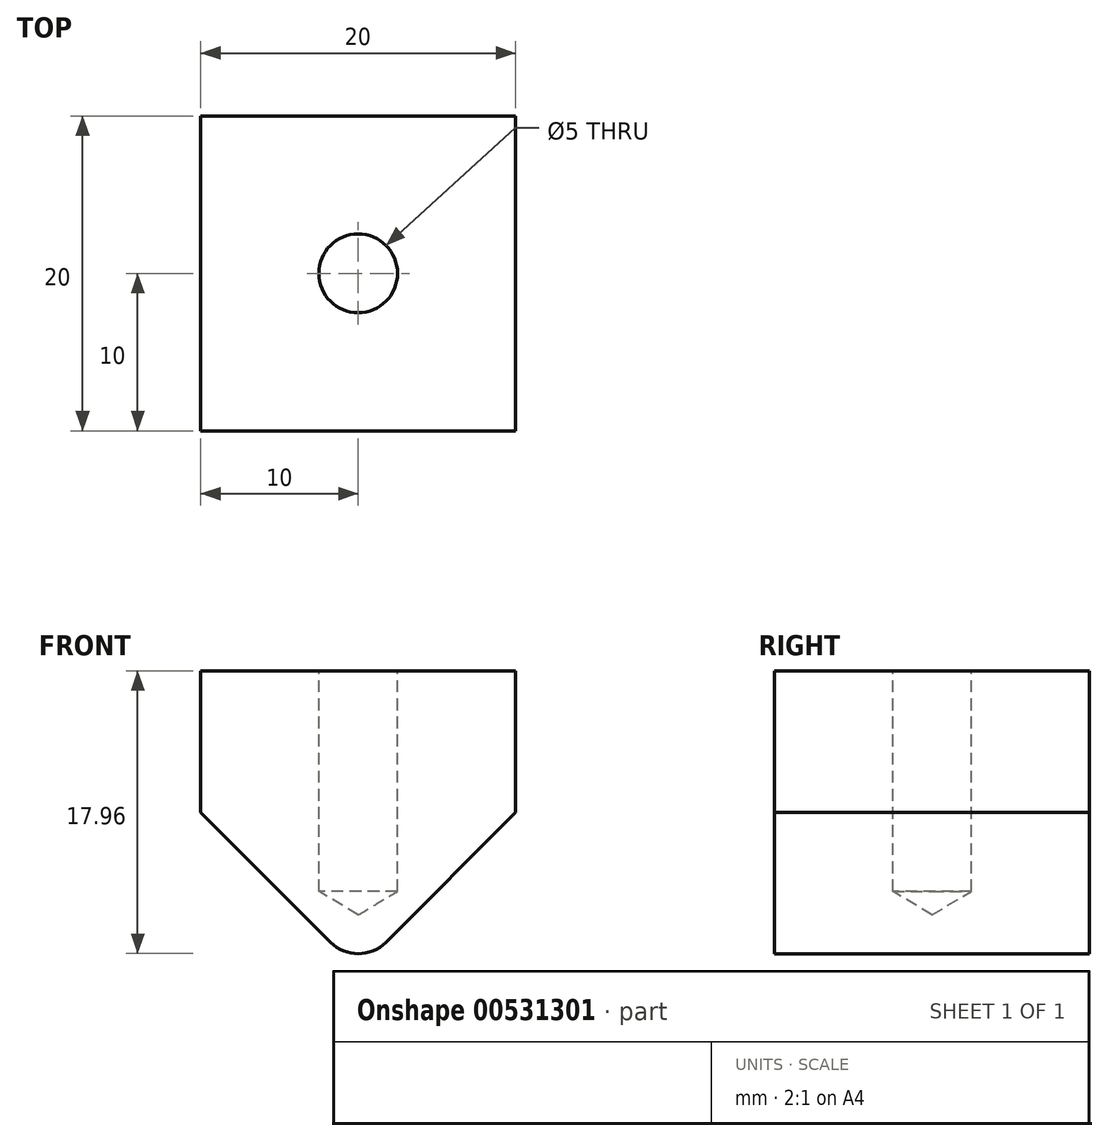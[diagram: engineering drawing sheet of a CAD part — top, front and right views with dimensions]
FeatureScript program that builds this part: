
annotation { "Feature Type Name" : "Feature", "Feature Type Description" : "" }
export const myFeature = defineFeature(function(context is Context, id is Id, definition is map)
    precondition{}
    {
        {
            var Q0;
            Q0=qCreatedBy(makeId("Front.planeOp"),FACE);
            var sketch = newSketch(context, id + "F0", { "sketchPlane" : qUnion([Q0])});
            skLineSegment(sketch, "E0", {"start": v(-14.02, 11.64) * mm, "end": v(5.98, 11.64) * mm});
            skLineSegment(sketch, "E1", {"start": v(5.98, 2.64) * mm, "end": v(5.98, 11.64) * mm});
            skLineSegment(sketch, "E2", {"start": v(5.98, 2.64) * mm, "end": v(-2.25, -5.6) * mm});
            skLineSegment(sketch, "E3", {"start": v(-5.79, -5.6) * mm, "end": v(-14.02, 2.64) * mm});
            skLineSegment(sketch, "E4", {"start": v(-14.02, 2.64) * mm, "end": v(-14.02, 11.64) * mm});
            skPoint(sketch, "E5.visualSharp", {"position": v(-4.02, -7.36) * mm});
            skArc(sketch, "E5.filletArc", {"start": v(-5.79, -5.6) * mm, "mid": v(-4.02, -6.32) * mm, "end": v(-2.25, -5.6) * mm});
            skSolve(sketch);
        }
        {
            var Q0;
            Q0=makeQuery(id+"F0.imprint","IMPRINT",FACE,{"disambiguationData":[TD([[makeQuery(id+"F0.imprint","IMPRINT",EDGE,{"derivedFrom":sQuery(id+"F0.wireOp",EDGE,"E0")}),-1.0]])]});
            extrude(context, id + "F1", {"entities" : qUnion([Q0]), "depth" : 20 * mm, "offsetDistance" : 25 * mm});
        }
        {
            var Q0;
            Q0=makeQuery(id+"F1.opExtrude","SWEPT_FACE",FACE,{"disambiguationData":[OSD([sQuery(id+"F0.wireOp",EDGE,"E0")])]});
            var sketch = newSketch(context, id + "F2", { "sketchPlane" : qUnion([Q0])});
            skPoint(sketch, "E6", {"position": v(-4.02, -10) * mm});
            skPoint(sketch, "E6.positionSnap0", {"position": v(5.98, -10) * mm});
            skPoint(sketch, "E6.positionSnap1", {"position": v(-4.02, 0) * mm});
            skSolve(sketch);
        }
        {
            var Q0;
            Q0=sQuery(id+"F2.wireOp",VERTEX,"E6");
            var Q1;
            Q1=makeQuery(id+"F1.opExtrude","SWEPT_BODY",BODY,{"disambiguationData":[OSD([sQuery(id+"F0.wireOp",EDGE,"E0"),sQuery(id+"F0.wireOp",EDGE,"E1"),sQuery(id+"F0.wireOp",EDGE,"E2"),sQuery(id+"F0.wireOp",EDGE,"E3"),sQuery(id+"F0.wireOp",EDGE,"E4"),sQuery(id+"F0.wireOp",EDGE,"E5.filletArc")])]});
            hole(context, id + "F3", {"style" : HoleStyle.SIMPLE, "endStyle" : HoleEndStyle.BLIND, "holeDiameter" : 5 * mm, "holeDepth" : 14 * mm, "isTappedThrough" : true, "tappedDepth" : 12 * mm, "tapClearance" : 3, "locations" : qUnion([Q0]), "scope" : qUnion([Q1])});
        }
    });
